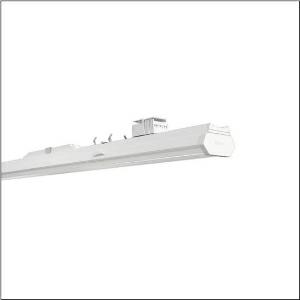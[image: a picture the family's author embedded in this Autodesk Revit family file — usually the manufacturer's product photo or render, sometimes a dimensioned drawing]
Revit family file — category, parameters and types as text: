
# Revit family: licross_21_protected_ho_52tp12dn4e5md
name_source: partatom
category: Lighting Fixtures
units: mm (PartAtom-declared; Revit-internal decimal feet)

## family parameters
Cut with Voids When Loaded = No
Host = Face
Light Source = No
Part Type = Normal
Room Calculation Point = No
Round Connector Dimension = Use Diameter
Shared = No

## types (1)
- --- (1 x LED, 2200 lm, 14.2 W, 4000K)
    Apparent Load = 14 VA
    CIE Flux Codes = 70 91 97 98 100
    Color Rendering = 80
    Color Temperature = 4000K
    Default Elevation = 1800 mm
    Description = Licross 21 Protected HO, luminaire insert, of sheet steel, galvanised, coil coated, white, length: 1.500mm, width: 90mm, height: 103mm, LED rated luminous flux: 14.690lm, light colour: 840, SDCM (Standard Deviation of Colour Matching)MacAdam ≤ 3 SDCM (initial), control gear: DALI 2 (for two DALI lines), with plug, 6-pole, with phase selection, mains connection: 220..240V, AC/DC, 0/50..60Hz, rated input power: 85W, without changeover relay, for emergency light function, for central battery installations according to EN 60598-2-22, internal wiring halogen-free, primary light control with lens, of plastic, primary optical cover: cover, of PMMA, light emission: direct distribution, primary light characteristic: symmetric, protection rating (complete): IP64, insulation class (complete): insulation class I (protective earthing), certification: CE, ENEC, VDE, UKCA, protection symbol: D if used in an environment with conductive dust loads with corresponding accessories, impact resistance: IK06, permissible ambient temperature for indoor applications: -25..+35°C, standard: EN 60598-2-22, corresponds to IFS (International Featured Standards) requirements for safety and quality in the food industry, reducing of maximum allowable ambient temperature of 5°C with ceiling mounting, LABS conformity tested according to VDMA 24364:2018-05, The light source and the operating device comply with the requirements of the Ecodesign Regulation (EU) 2019/2020 and are replaceable in accordance with this regulation, packaging unit: 1 piece
    Height = 92 mm
    Lamp = 1 x LED
    Lamp Light Flux = 2200 lm
    Lamp Power = 14.2 W
    Lamp count = 1
    Length = 1500 mm
    Luminous efficacy = 155 lm/W
    Manufacturer = Siteco
    ModVariant = No
    Model = 52TP12DN4E5MD
    Mounting Place = Ceiling
    Mounting Type = Pendant
    Number of Poles = 1
    OnlyDefault = Yes
    Power Factor = 1
    Product Name = Licross 21 Protected HO
    Product group = luminaire insert | ceiling pendant
    ProductGroupID = 901
    Protection Class = Protection class I
    Protection Degree = IP 64
    RLX_Detail_Level = 1
    RLX_Emergency_Light_Flux = 0 lm
    RLX_Emergency_Type = 0
    RLX_Emergency_Type_DB = No
    RlxData = <blob elided: 25117 chars, md5=c0d8a11d>
    Socket = socket
    Standby Power = 0 W
    System Light Flux = 2200 lm
    System Power = 14 W
    Type Comments = : DC mode (central or group accumulator) initial emergency light level
    Type Image = l_1256148.jpg
    URL = http://relux.com
    VarID = @adj_116513
    Voltage = 0 V
    Weight = 0.00 kg
    Width = 88 mm

## geometry (parser evidence)
native form markers: Blend x4, Sweep x10
no freeform markers — native parametric forms only
